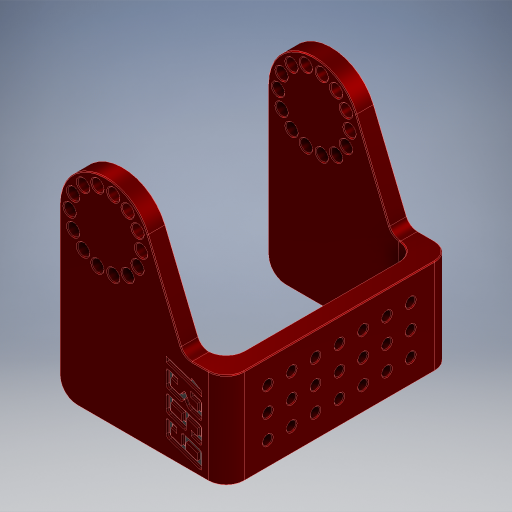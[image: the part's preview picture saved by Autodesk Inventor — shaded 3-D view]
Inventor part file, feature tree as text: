
AUTODESK INVENTOR PART (.ipt)
format: ipt  version: 2024.2 (Build 282272000, 272)  size: 1,319,424 bytes
history: native  units: in
note: dims shown in document units (in); Inventor stores cm internally (conversion verified against a paired STEP export)
features: sketch x7, extrude x7, fillet x3, projected_geometry x3, chamfer x2, plane x1, thicken_offset x1, pattern_linear x1
ambient origin geometry x8: Origin, YZ Plane, XZ Plane, XY Plane, X Axis, Y Axis, Z Axis, Center Point
bodies: Body1 (feature_tree)
feature tree (25):
  sketch  "Sketch6"  dims[d44=1.5in d45=0.25in]
  plane  "Work Plane5"
  extrude  "Extrusion6"  Depth=0.25in
  extrude  "Extrusion7"  Depth=1.925in
  extrude  "Extrusion8"  Depth=1.0in
  extrude  "Extrusion9"  Depth=4.0in
  thicken_offset  "Thicken1"
  fillet  "Fillet1"  Radius=0.125in
  chamfer  "Chamfer1"  Distance=0.125in
  extrude  "Extrusion10"  Depth=1.0in TaperAngle=0.0deg
  chamfer  "Chamfer2"  Distance=0.375in
  pattern_linear  "Rectangular Pattern1"  Spacing1=0.0156in  [1 undecoded]
  sketch  "Sketch12"  dims[d63=0.25in]
  extrude  "Extrusion11"  Depth=0.0197in
  extrude  "Extrusion12"  Depth=0.0197in
  fillet  "Fillet3"  Radius=0.5in
  fillet  "Fillet4"  Radius=1.1811in
  sketch  "Sketch7"  dims[d46=5.5118in d48=360.0deg d50=1.925in]
  sketch  "Sketch8"  dims[d51=3.25in d52=1.0in]
  projected_geometry  "Projected Loop3"
  projected_geometry  "Projected Loop4"
  sketch  "Sketch9"  dims[d53=0.25in d54=4.0in d55=0.125in d56=0.0in d57=0.125in d58=0.0in]
  projected_geometry  "Projected Loop5"
  sketch  "Sketch10"  dims[d59=0.125in d60=0.0in d61=1.0in d62=0.0in]
  sketch  "Sketch13"  dims[d64=0.25in d65=0.375in d67=0.0156in d68=0.125in d69=45.0deg d70=0.196in d71=0.5in d72=0.5in d73=1.1811in d75=0.5in d76=2.7559in d78=0.5in d81=0.8125in d82=0.0in d83=0.0156in d84=0.125in d85=45.0deg d86=1.1811in d88=0.5in d89=2.7559in d91=0.5in d92=0.0591in d93=0.0in d94=0.0591in d95=0.0in d96=0.0197in d97=0.0197in d42=0.5in d43=0.0344in]
note: 1 required parameter value undecoded (feature->parameter linkage not recoverable at this tier; creation-order binding heuristic only, values carry confidence <= 0.55)
